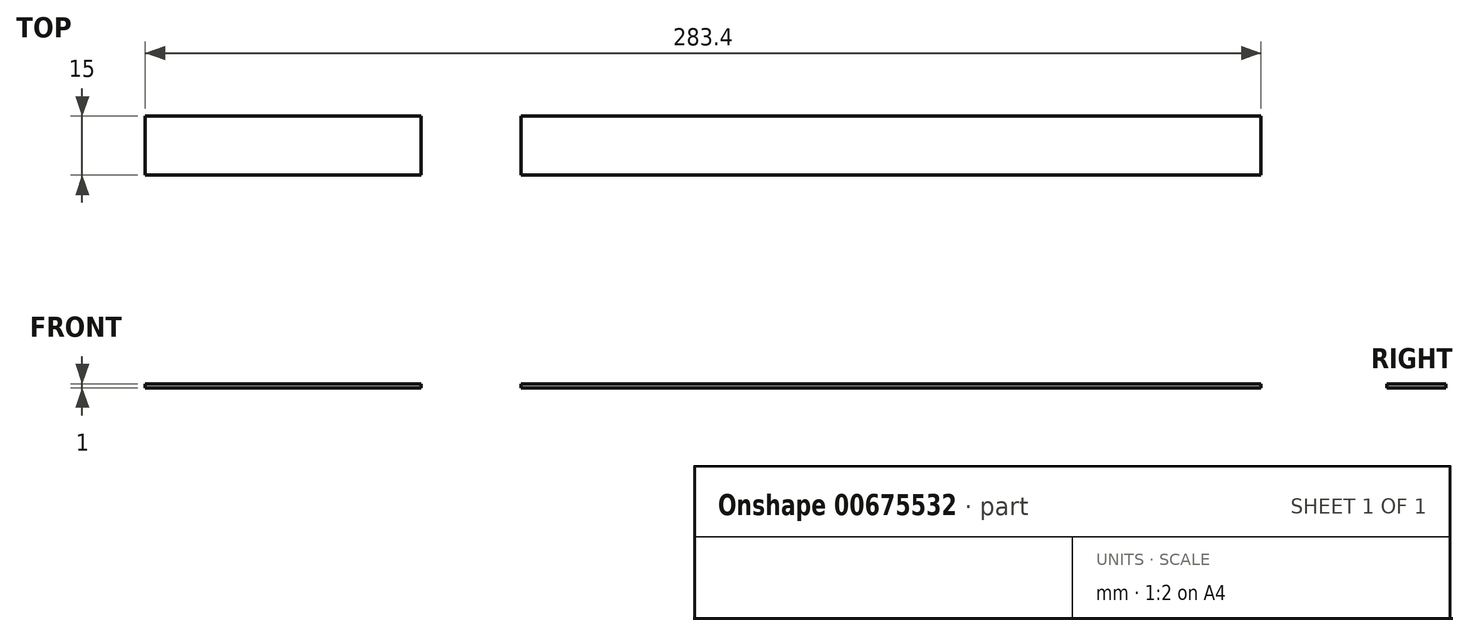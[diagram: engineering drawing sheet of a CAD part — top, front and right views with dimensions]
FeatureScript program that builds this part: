
annotation { "Feature Type Name" : "Feature", "Feature Type Description" : "" }
export const myFeature = defineFeature(function(context is Context, id is Id, definition is map)
    precondition{}
    {
        {
            var Q0;
            Q0=qCreatedBy(makeId("Top.planeOp"),FACE);
            var sketch = newSketch(context, id + "F0", { "sketchPlane" : qUnion([Q0])});
            skLineSegment(sketch, "E0.bottom", {"start": v(-141.7, 7.5) * mm, "end": v(-71.7, 7.5) * mm});
            skLineSegment(sketch, "E0.top", {"start": v(-141.7, -7.5) * mm, "end": v(-71.7, -7.5) * mm});
            skLineSegment(sketch, "E0.left", {"start": v(-141.7, 7.5) * mm, "end": v(-141.7, -7.5) * mm});
            skLineSegment(sketch, "E0.right", {"start": v(141.7, 7.5) * mm, "end": v(141.7, -7.5) * mm});
            skLineSegment(sketch, "E1", {"start": v(-46.3, -7.5) * mm, "end": v(141.7, -7.5) * mm});
            skLineSegment(sketch, "E2", {"start": v(-71.7, -7.5) * mm, "end": v(-71.7, 7.5) * mm});
            skLineSegment(sketch, "E3", {"start": v(-46.3, -7.5) * mm, "end": v(-46.3, 7.5) * mm});
            skLineSegment(sketch, "E4.trimOffspring", {"start": v(-46.3, 7.5) * mm, "end": v(141.7, 7.5) * mm});
            skSolve(sketch);
        }
        {
            var Q0;
            Q0 = qSketchRegion(id + "F0", true);
            extrude(context, id + "F1", {"entities" : qUnion([Q0]), "depth" : 1 * mm, "offsetDistance" : 25 * mm});
        }
    });
